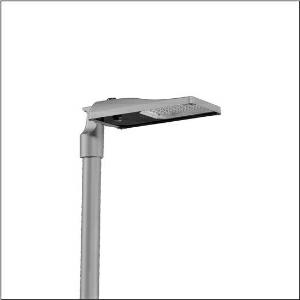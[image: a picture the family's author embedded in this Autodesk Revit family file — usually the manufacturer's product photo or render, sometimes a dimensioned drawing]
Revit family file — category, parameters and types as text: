
# Revit family: streetlight_sl_31_mini___p0_5a_5xh6v31t08ja_e515
name_source: partatom
category: Lighting Fixtures
units: mm (PartAtom-declared; Revit-internal decimal feet)

## family parameters
Cut with Voids When Loaded = No
Host = Face
Light Source = No
Part Type = Normal
Room Calculation Point = No
Round Connector Dimension = Use Diameter
Shared = No

## types (1)
- --- (1 x LED, 12050 lm, 82.5 W, 3000K)
    Apparent Load = 83 VA
    CIE Flux Codes = 37 73 96 100 100
    Color Rendering = 70
    Color Temperature = 3000K
    Default Elevation = 1800 mm
    Description = Streetlight SL 31 mini D4i, Desk-Remote mast luminaire for post-top, side-entry; light control with lens of PMMA; light distribution: P0.5a, direct asymmetric distribution, for standard-compliant lighting for roads and squares; LED: luminous flux: 12.050lm, light colour: 730, colour temperature: 3000K; luminous efficacy: 146,1lm/W; control: pre-setting: logarithmic dimming characteristic, flexible luminous flux parameterisation, time-dependent luminous flux control, constant luminous flux control, power reduction, intelligent temperature release in ECG and LED module, overheat protection; luminaire housing, of diecast aluminium, SITECO metallic grey (DB 702S), corrosivity category C5 high according to DIN EN ISO 12944; cover of toughened safety glass, transparent, opened without tools; mast flange of diecast aluminium, SITECO metallic grey (DB 702S), spigot size: 76/60mm, mast flange included unmounted; cable length: 10,5m, connection cable pre-assembled; mains connection: 220..240V, AC, 50/60Hz; power consumption (at start of service life): 82,5W / (at end of service life): 90,1W / (with reduced operation 50%): 36,8W; protection rating (complete): IP66; insulation class (complete): insulation class II (safety insulation); impact resistance: IK09; certification: CE, ENEC, ENEC+, VDE, UKCA, ZD4i; permissible operating ambient temperature for outdoor applications: -40..+50°C; packaging unit: 1 piece

Light Distribution: P0.5a
    Height = 76 mm
    Lamp = 1 x LED
    Lamp Light Flux = 12050 lm
    Lamp Power = 82.5 W
    Lamp count = 1
    Length = 547 mm
    Luminous efficacy = 146 lm/W
    Manufacturer = Siteco
    ModVariant = No
    Model = 5XH6V31T08JA
    Number of Poles = 1
    OnlyDefault = Yes
    Power Factor = 1
    Product Name = Streetlight SL 31 mini | P0.5a
    Product group = mast luminaire | pylon top
    ProductGroupID = 6100
    Protection Class = Protection class II
    Protection Degree = IP 66
    RLX_Detail_Level = 1
    RLX_Emergency_Light_Flux = 0 lm
    RLX_Emergency_Type = 0
    RLX_Emergency_Type_DB = No
    RlxData = <blob elided: 39685 chars, md5=fa2c0721>
    Socket = socket
    Standby Power = 0 W
    System Light Flux = 12050 lm
    System Power = 83 W
    Type Comments = factory setting: luminous flux: 100 % | dim-lin: 254 | 870 mA
    Type Image = l_1300332.jpg
    URL = http://relux.com
    VarID = @adj_064881
    Voltage = 0 V
    Weight = 0.00 kg
    Width = 265 mm

## geometry (parser evidence)
native form markers: Blend x4, Sweep x9
no freeform markers — native parametric forms only
